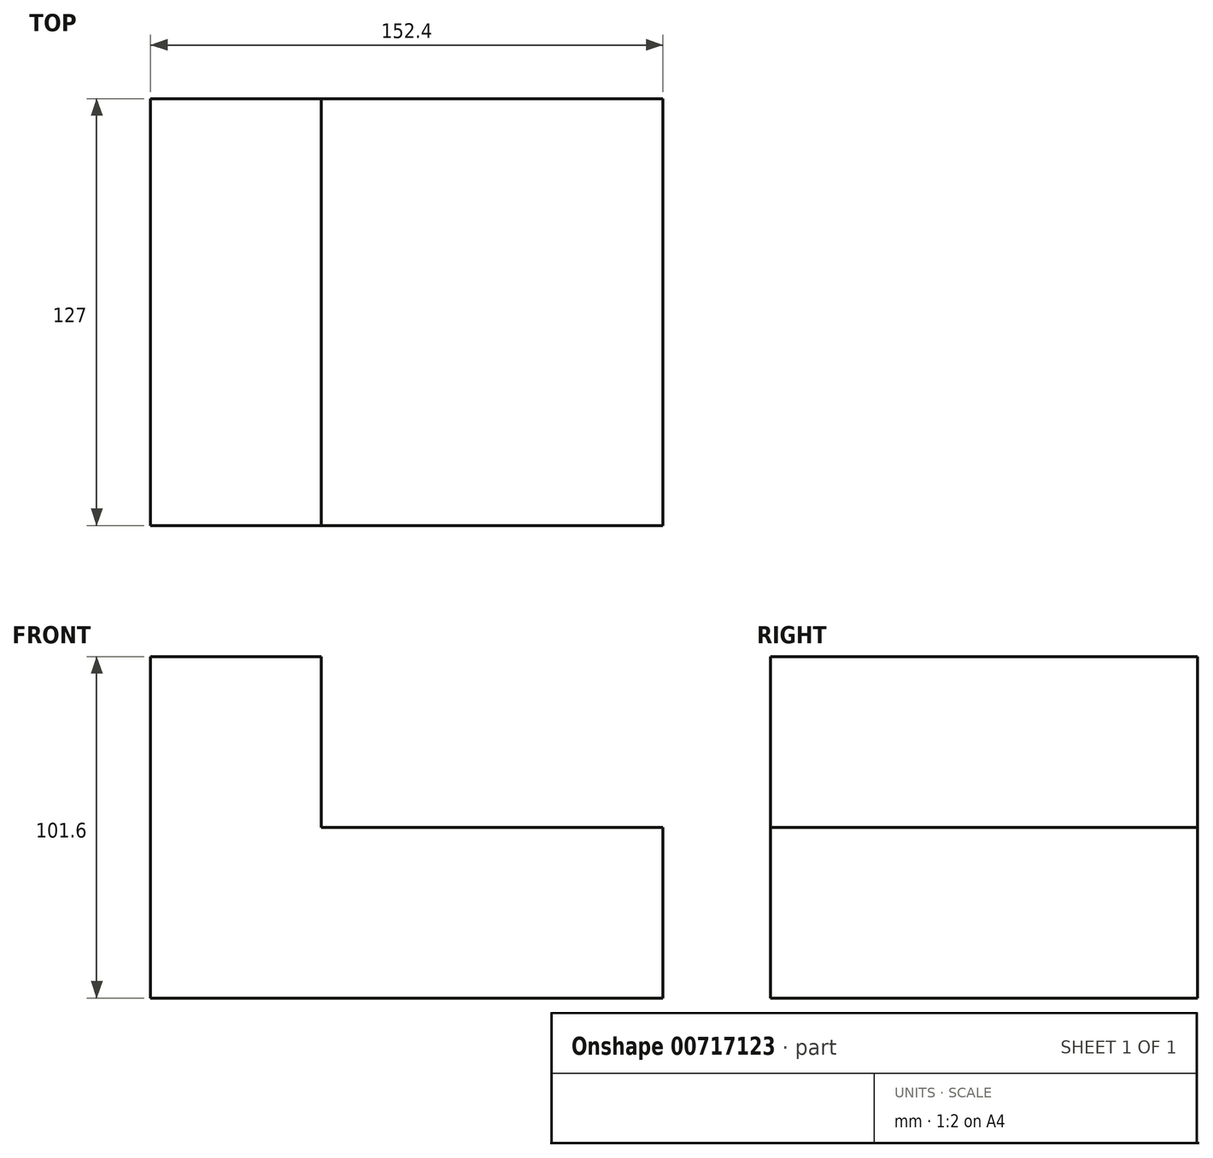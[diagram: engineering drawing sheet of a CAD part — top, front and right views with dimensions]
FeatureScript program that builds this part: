
annotation { "Feature Type Name" : "Feature", "Feature Type Description" : "" }
export const myFeature = defineFeature(function(context is Context, id is Id, definition is map)
    precondition{}
    {
        {
            var Q0;
            Q0=qCreatedBy(makeId("Front.planeOp"),FACE);
            var sketch = newSketch(context, id + "F0", { "sketchPlane" : qUnion([Q0])});
            skLineSegment(sketch, "E0", {"start": v(-118.7, -67.02) * mm, "end": v(33.7, -67.02) * mm});
            skLineSegment(sketch, "E1", {"start": v(33.7, -67.02) * mm, "end": v(33.7, -16.22) * mm});
            skLineSegment(sketch, "E2", {"start": v(33.7, -16.22) * mm, "end": v(-67.9, -16.22) * mm});
            skLineSegment(sketch, "E3", {"start": v(-67.9, -16.22) * mm, "end": v(-67.9, 34.58) * mm});
            skLineSegment(sketch, "E4", {"start": v(-67.9, 34.58) * mm, "end": v(-118.7, 34.58) * mm});
            skLineSegment(sketch, "E5", {"start": v(-118.7, 34.58) * mm, "end": v(-118.7, -67.02) * mm});
            skSolve(sketch);
        }
        {
            var Q0;
            Q0=makeQuery(id+"F0.imprint","IMPRINT",FACE,{"disambiguationData":[TD([[makeQuery(id+"F0.imprint","IMPRINT",EDGE,{"derivedFrom":sQuery(id+"F0.wireOp",EDGE,"E0")}),1.0]])]});
            extrude(context, id + "F1", {"entities" : qUnion([Q0]), "depth" : 127 * mm, "offsetDistance" : 25.4 * mm});
        }
    });
